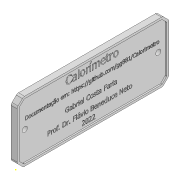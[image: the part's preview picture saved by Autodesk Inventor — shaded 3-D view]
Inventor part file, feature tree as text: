
AUTODESK INVENTOR PART (.ipt)
format: ipt  version: 2020 (Build 240168000, 168)  size: 3,386,368 bytes
history: native  units: mm
features: sketch x5, extrude x4, other x2, chamfer x1, fillet x1
ambient origin geometry x8: Origin, YZ Plane, XZ Plane, XY Plane, X Axis, Y Axis, Z Axis, Center Point
bodies: Body1 (feature_tree)
feature tree (13):
  other  "Sólido1"
  extrude  "Extrusão1"  Depth=100.0mm
  extrude  "Extrusão2"  Depth=3.5mm
  extrude  "Extrusão3"  Depth=6.0mm
  chamfer  "Chanfro1"  Distance=4.0mm
  fillet  "Arredondamento1"  Radius=40.0mm
  sketch  "Esboço4"  dims[d7=6.0mm d8=4.0mm d9=0.0mm d10=40.0mm]
  sketch  "Esboço5"  dims[d11=20.0mm d12=20.0mm d13=1.0mm d14=0.0mm d15=4.0mm d16=2.0mm d17=45.0deg d18=2.0mm d19=1.0mm d20=0.0mm]
  extrude  "Extrusão4"  Depth=1.0mm
  sketch  "Esboço1"  dims[d0=100.0mm d1=40.0mm]
  sketch  "Esboço2"  dims[d2=3.0mm d3=0.0mm d4=3.5mm]
  sketch  "Esboço3"  dims[d5=3.5mm d6=6.0mm]
  other  "Contorno projetado1"
